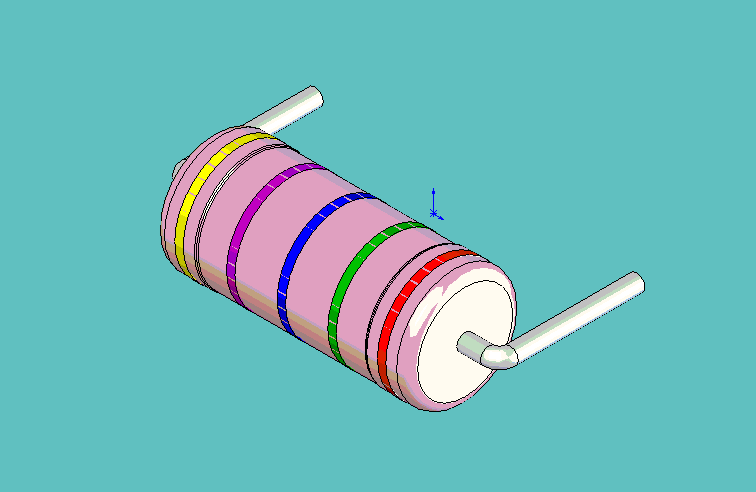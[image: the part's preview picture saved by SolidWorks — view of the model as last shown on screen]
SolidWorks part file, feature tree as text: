
SOLIDWORKS PART (.sldprt)
format: sldprt  version: not decoded by parser v0  size: 324,608 bytes
history: native  units: mm
features: sketch x9, plane x7, extrude x6, fillet x3, material x1, cut_extrude x1, sweep x1, mirror x1 (+10 scaffold rows collapsed)
feature tree (39):
  scaffold x10  (default folders/planes/origin — collapsed)
  material  "材质 <未指定>"
  plane  "前视基准面"
  plane  "上视基准面"
  plane  "右视基准面"
  sketch  "草图1"  dims[D1=5.5mm D2=4.5mm]
  extrude  "拉伸1"  Depth=12mm
  sketch  "草图5"  dims[D1=0.05mm]
  cut_extrude  "切除-拉伸2"  Depth=8mm
  fillet  "圆角10"  Radius=0.1mm
  fillet  "圆角11"  Radius=0.1mm
  fillet  "圆角13"  Radius=0.5mm
  plane  "基准面2"  Offset=2.4mm
  plane  "基准面3"  Offset=4.8mm
  plane  "基准面4"  Offset=2.4mm
  plane  "基准面5"  Offset=4.8mm
  sketch  "草图6"  dims[D1=0.01mm]
  extrude  "拉伸2"  Depth=0.4mm
  sketch  "草图7"
  extrude  "拉伸3"  Depth=0.4mm
  sketch  "草图8"  dims[D1=0.01mm]
  extrude  "拉伸4"  Depth=0.4mm
  sketch  "草图9"
  extrude  "拉伸5"  Depth=0.4mm
  sketch  "草图10"
  extrude  "拉伸6"  Depth=0.4mm
  sketch  "草图12"  dims[D6=0.5mm D1=7.62mm D2=2.54mm D3=2.0mm D4=2.0mm D5=2.0mm]
  sketch  "草图13"  dims[D1=0.8mm]
  sweep  "扫描1"
  mirror  "镜向3"
decode coverage: 16 of 21 modeling features carry decoded parameters
note: suppression state not decoded; provenance and decode notes live in map.json
